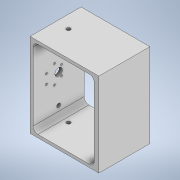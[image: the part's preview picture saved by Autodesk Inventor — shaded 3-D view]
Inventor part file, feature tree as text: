
AUTODESK INVENTOR PART (.ipt)
format: ipt  version: 2020.3 (Build 243373000, 373)  size: 206,336 bytes
history: native  units: mm
features: extrude x9, sketch x9, projected_geometry x3, fillet x2
ambient origin geometry x8: Origin, YZ Plane, XZ Plane, XY Plane, X Axis, Y Axis, Z Axis, Center Point
bodies: Solid1 (feature_tree)
feature tree (23):
  extrude  "Extrusion1"  Depth=130.0mm
  extrude  "Extrusion5"  Depth=5.0mm TaperAngle=0.0deg
  extrude  "Extrusion6"  Depth=140.0mm
  extrude  "Extrusion8"  Depth=70.0mm
  extrude  "Extrusion9"  Depth=2.778mm TaperAngle=0.0deg
  fillet  "Fillet1"  Radius=17.5mm
  fillet  "Fillet2"  Radius=17.5mm
  extrude  "Extrusion10"  Depth=8.0mm
  extrude  "Extrusion12"  Depth=3.3mm
  sketch  "Sketch12"  dims[d33=37.767mm d34=78.237mm]
  sketch  "Sketch13"  dims[d35=3.3mm d36=37.733mm d38=61.753708mm d39=3.3mm d41=85.5mm d42=49.5mm d43=3.3mm d44=54.5mm d45=3.3mm d46=77.75mm d47=62.923mm d48=3.3mm d49=62.25mm d50=62.923mm d51=5.0mm d52=0.0mm d53=6.5mm d54=6.5mm d58=21.5mm d59=21.5mm d60=10.0mm d61=0.0mm d62=6.5mm d63=21.5mm d64=10.0mm d65=0.0mm d66=6.5mm d67=21.5mm d68=10.0mm d69=0.0mm]
  extrude  "Extrusion13"  Depth=78.237mm
  extrude  "Extrusion14"  Depth=10.0mm
  sketch  "Sketch1"  dims[d0=101.968mm d1=130.0mm]
  sketch  "Sketch5"  dims[d2=5.0mm d3=50.0mm d4=0.0mm]
  sketch  "Sketch6"  dims[d14=140.0mm d15=24.0mm]
  projected_geometry  "Projected Loop4"
  sketch  "Sketch8"  dims[d16=25.0mm d17=70.0mm]
  projected_geometry  "Projected Loop5"
  sketch  "Sketch9"  dims[d18=2.778mm d19=0.0mm d20=2.778mm d21=0.0mm d25=17.5mm d26=0.0mm d27=17.5mm d28=0.0mm]
  projected_geometry  "Projected Loop6"
  sketch  "Sketch10"  dims[d29=8.0mm d30=8.0mm]
  sketch  "Sketch11"  dims[d31=12.5mm d32=3.3mm]
